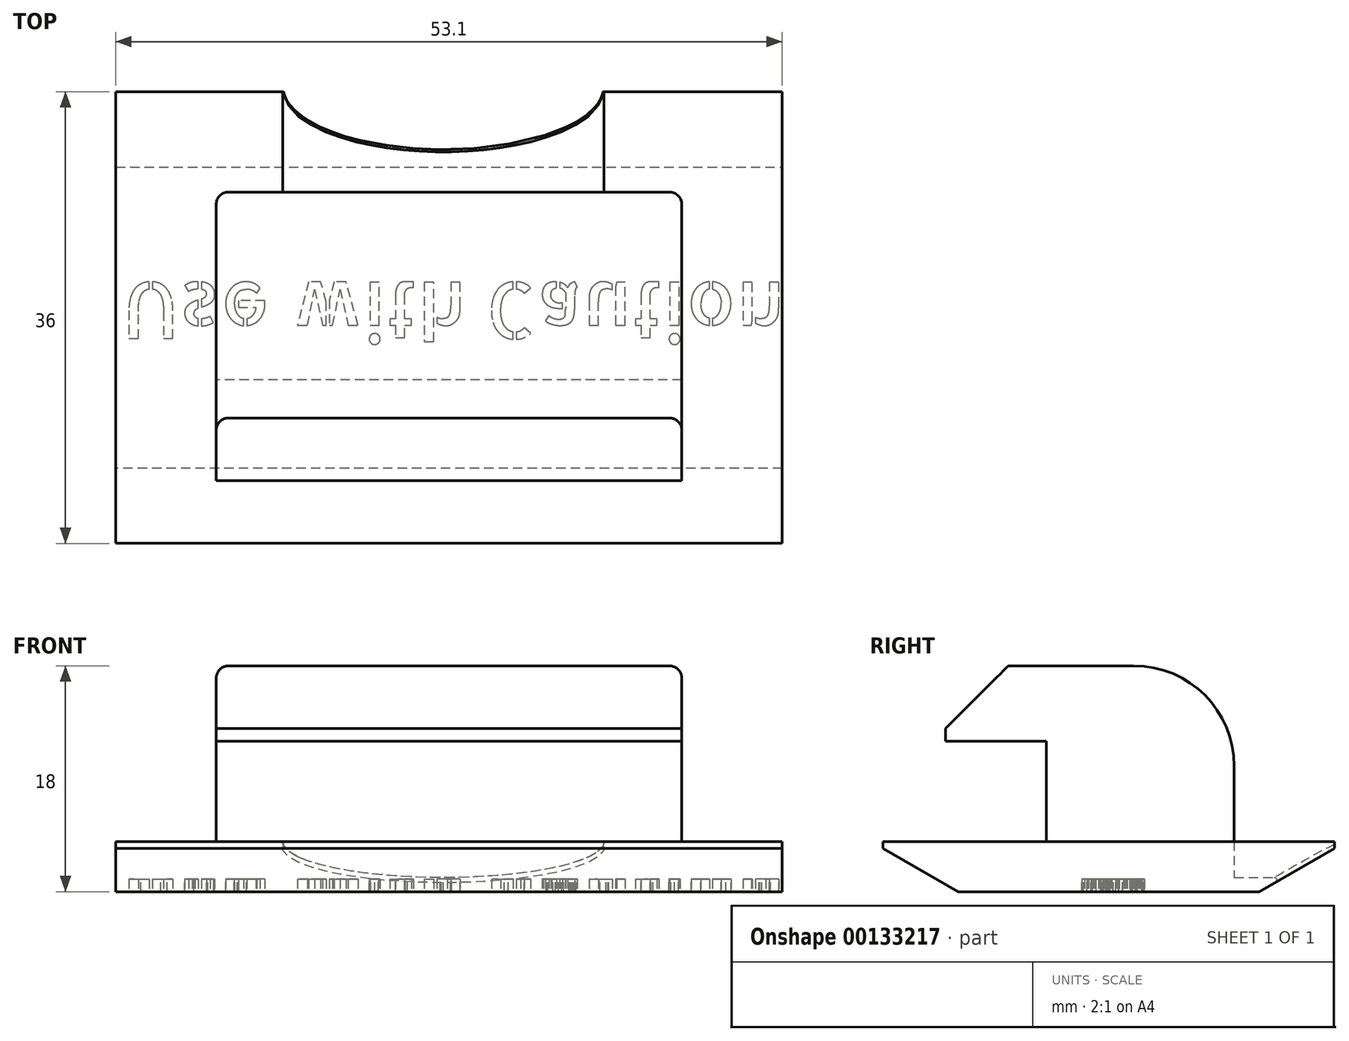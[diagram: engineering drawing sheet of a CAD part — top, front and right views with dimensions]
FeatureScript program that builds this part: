
annotation { "Feature Type Name" : "Feature", "Feature Type Description" : "" }
export const myFeature = defineFeature(function(context is Context, id is Id, definition is map)
    precondition{}
    {
        {
            var Q0;
            Q0=qCreatedBy(makeId("Top.planeOp"),FACE);
            var sketch = newSketch(context, id + "F0", { "sketchPlane" : qUnion([Q0])});
            skLineSegment(sketch, "E0.bottom", {"start": v(-18.1, 7.47) * mm, "end": v(19, 7.47) * mm});
            skLineSegment(sketch, "E0.top", {"start": v(-18.1, -12.53) * mm, "end": v(19, -12.53) * mm});
            skLineSegment(sketch, "E0.left", {"start": v(-18.1, 7.47) * mm, "end": v(-18.1, -12.53) * mm});
            skLineSegment(sketch, "E0.right", {"start": v(19, 7.47) * mm, "end": v(19, -12.53) * mm});
            skLineSegment(sketch, "E1.0", {"start": v(27, 15.47) * mm, "end": v(27, -20.53) * mm});
            skLineSegment(sketch, "E1.1", {"start": v(-26.1, 15.47) * mm, "end": v(27, 15.47) * mm});
            skLineSegment(sketch, "E1.2", {"start": v(-26.1, 15.47) * mm, "end": v(-26.1, -20.53) * mm});
            skLineSegment(sketch, "E1.3", {"start": v(-26.1, -20.53) * mm, "end": v(27, -20.53) * mm});
            skSolve(sketch);
        }
        {
            var Q0;
            Q0=makeQuery(id+"F0.imprint","IMPRINT",FACE,{"disambiguationData":[TD([[makeQuery(id+"F0.imprint","IMPRINT",EDGE,{"derivedFrom":sQuery(id+"F0.wireOp",EDGE,"E0.bottom")}),-1.0]])]});
            extrude(context, id + "F1", {"entities" : qUnion([Q0]), "depth" : 18 * mm});
        }
        {
            var Q0;
            Q0=makeQuery(id+"F0.imprint","IMPRINT",FACE,{"disambiguationData":[TD([[makeQuery(id+"F0.imprint","IMPRINT",EDGE,{"derivedFrom":sQuery(id+"F0.wireOp",EDGE,"E0.bottom")}),1.0]])]});
            extrude(context, id + "F2", {"entities" : qUnion([Q0]), "operationType" : NewBodyOperationType.ADD, "depth" : 4 * mm});
        }
        {
            var Q0;
            Q0=makeQuery(id+"F2.opExtrude","CAP_EDGE",EDGE,{"disambiguationData":[OSD([sQuery(id+"F0.wireOp",EDGE,"E1.1")])],"isStart":true});
            var Q1;
            Q1=makeQuery(id+"F2.opExtrude","CAP_EDGE",EDGE,{"disambiguationData":[OSD([sQuery(id+"F0.wireOp",EDGE,"E1.3")])],"isStart":true});
            chamfer(context, id + "F3", {"entities" : qUnion([Q0, Q1]), "chamferType" : ChamferType.OFFSET_ANGLE, "width" : 6 * mm, "oppositeDirection" : false, "angle" : 30 * degree, "tangentPropagation" : true});
        }
        {
            var Q0;
            Q0=makeQuery(id+"F1.opExtrude","SWEPT_FACE",FACE,{"disambiguationData":[OSD([sQuery(id+"F0.wireOp",EDGE,"E0.left")])]});
            var sketch = newSketch(context, id + "F4", { "sketchPlane" : qUnion([Q0])});
            skLineSegment(sketch, "E2.bottom", {"start": v(12.53, 12) * mm, "end": v(7.5, 12) * mm});
            skLineSegment(sketch, "E2.top", {"start": v(12.53, 4) * mm, "end": v(7.5, 4) * mm});
            skLineSegment(sketch, "E2.left", {"start": v(12.53, 12) * mm, "end": v(12.53, 4) * mm});
            skLineSegment(sketch, "E2.right", {"start": v(7.5, 12) * mm, "end": v(7.5, 4) * mm});
            skSolve(sketch);
        }
        {
            var Q0;
            Q0=makeQuery(id+"F4.imprint","IMPRINT",FACE,{"disambiguationData":[TD([[makeQuery(id+"F4.imprint","IMPRINT",EDGE,{"derivedFrom":sQuery(id+"F4.wireOp",EDGE,"E2.bottom")}),1.0]])]});
            extrude(context, id + "F5", {"entities" : qUnion([Q0]), "operationType" : NewBodyOperationType.REMOVE, "oppositeDirection" : true, "depth" : 40 * mm});
        }
        {
            var Q0;
            Q0=makeQuery(id+"F2.opExtrude","SWEPT_FACE",FACE,{"disambiguationData":[OSD([sQuery(id+"F0.wireOp",EDGE,"E1.1")])]});
            var sketch = newSketch(context, id + "F6", { "sketchPlane" : qUnion([Q0])});
            skEllipse(sketch, "E3", {"center": v(0, 4) * mm, "majorRadius": 12.8 * mm, "minorRadius": 2.88 * mm, "majorAxis": v(-1, 0)});
            skSolve(sketch);
        }
        {
            var Q0;
            {var subQ0=sQuery(id+"F6.wireOp",EDGE,"E3");var subQ1=sQuery(id+"F0.wireOp",EDGE,"E1.1");var subQ2=makeQuery(id+"F3.opChamfer","BLEND_EDGE",EDGE,{"blendedFrom":[makeQuery(id+"F2.opExtrude","CAP_EDGE",EDGE,{"disambiguationData":[OSD([subQ1])],"isStart":true}),makeQuery(id+"F2.opExtrude","SWEPT_FACE",FACE,{"disambiguationData":[OSD([subQ1])]})],"blendedInto":[makeQuery(id+"F2.opExtrude","SWEPT_FACE",FACE,{"disambiguationData":[OSD([subQ1])]})]});var subQ3=makeQuery(id+"F6.imprint","INTERSECT",VERTEX,{"disambiguationData":[OD(0.0)],"derivedFrom":[subQ2,subQ0]});Q0=makeQuery(id+"F6.imprint","IMPRINT",FACE,{"disambiguationData":[TD([[makeQuery(id+"F6.imprint","IMPRINT",EDGE,{"disambiguationData":[TD([[subQ3,-1.0]])],"derivedFrom":subQ0}),1.0]])]});}
            var Q1;
            {var subQ0=sQuery(id+"F6.wireOp",EDGE,"E3");var subQ1=sQuery(id+"F0.wireOp",EDGE,"E1.1");var subQ4=makeQuery(id+"F2.opExtrude","CAP_EDGE",EDGE,{"disambiguationData":[OSD([subQ1])],"isStart":false});var subQ5=makeQuery(id+"F6.imprint","INTERSECT",VERTEX,{"disambiguationData":[OD(0.0)],"derivedFrom":[subQ4,subQ0]});Q1=makeQuery(id+"F6.imprint","IMPRINT",FACE,{"disambiguationData":[TD([[makeQuery(id+"F6.imprint","IMPRINT",EDGE,{"disambiguationData":[TD([[subQ5,1.0]])],"derivedFrom":subQ4}),1.0]])]});}
            extrude(context, id + "F7", {"entities" : qUnion([Q0, Q1]), "operationType" : NewBodyOperationType.REMOVE, "oppositeDirection" : true, "depth" : 8 * mm});
        }
        {
            var Q0;
            Q0=makeQuery(id+"F1.opExtrude","SWEPT_FACE",FACE,{"disambiguationData":[OSD([sQuery(id+"F0.wireOp",EDGE,"E0.top")])]});
            extrude(context, id + "F8", {"entities" : qUnion([Q0]), "operationType" : NewBodyOperationType.ADD, "depth" : 3 * mm});
        }
        {
            var Q0;
            Q0=makeQuery(id+"F8.opExtrude","CAP_EDGE",EDGE,{"disambiguationData":[OSD([sQuery(id+"F0.wireOp",EDGE,"E0.top")])],"isStart":false});
            chamfer(context, id + "F9", {"entities" : qUnion([Q0]), "width" : 5 * mm, "tangentPropagation" : true});
        }
        {
            var Q0;
            Q0=makeQuery(id+"F1.opExtrude","CAP_EDGE",EDGE,{"disambiguationData":[OSD([sQuery(id+"F0.wireOp",EDGE,"E0.bottom")])],"isStart":false});
            fillet(context, id + "F10", {"entities" : qUnion([Q0]), "radius" : 8 * mm, "tangentPropagation" : true, "allowEdgeOverflow" : false});
        }
        {
            var Q0;
            {var subQ0=sQuery(id+"F0.wireOp",EDGE,"E0.right");var subQ1=sQuery(id+"F0.wireOp",EDGE,"E0.left");var subQ2=sQuery(id+"F0.wireOp",EDGE,"E0.top");var subQ3=sQuery(id+"F0.wireOp",EDGE,"E0.bottom");Q0=makeQuery(id+"F2.boolean.opBoolean","MERGE",FACE,{"derivedFrom":[makeQuery(id+"F1.opExtrude","CAP_FACE",FACE,{"disambiguationData":[OSD([subQ3,subQ2,subQ1,subQ0])],"isStart":true}),makeQuery(id+"F2.opExtrude","CAP_FACE",FACE,{"disambiguationData":[OSD([subQ3,subQ2,subQ1,subQ0,sQuery(id+"F0.wireOp",EDGE,"E1.0"),sQuery(id+"F0.wireOp",EDGE,"E1.1"),sQuery(id+"F0.wireOp",EDGE,"E1.2"),sQuery(id+"F0.wireOp",EDGE,"E1.3")])],"isStart":true})]});}
            var sketch = newSketch(context, id + "F11", { "sketchPlane" : qUnion([Q0])});
            skText(sketch, "E4", { "text": "Use with Caution\n", "fontName": "AllertaStencil-Regular.ttf"});
            const initialGuessF11  = {"E4": [-0.02555, -0.0003, 1, 0, 0.0045]};
            skSetInitialGuess(sketch, initialGuessF11);
            skSolve(sketch);
        }
        {
            var Q0;
            Q0 = qSketchRegion(id + "F11", true);
            extrude(context, id + "F12", {"entities" : qUnion([Q0]), "operationType" : NewBodyOperationType.REMOVE, "oppositeDirection" : true, "depth" : 1 * mm});
        }
        {
            var Q0;
            Q0=makeQuery(id+"F1.opExtrude","SWEPT_EDGE",EDGE,{"disambiguationData":[OSD([sQuery(id+"F0.wireOp",EDGE,"E0.bottom"),sQuery(id+"F0.wireOp",EDGE,"E0.right")])]});
            var Q1;
            Q1=makeQuery(id+"F1.opExtrude","CAP_EDGE",EDGE,{"disambiguationData":[OSD([sQuery(id+"F0.wireOp",EDGE,"E0.right")])],"isStart":false});
            var Q2;
            Q2=makeQuery(id+"F1.opExtrude","CAP_EDGE",EDGE,{"disambiguationData":[OSD([sQuery(id+"F0.wireOp",EDGE,"E0.bottom")])],"isStart":false});
            var Q3;
            Q3=makeQuery(id+"F1.opExtrude","SWEPT_EDGE",EDGE,{"disambiguationData":[OSD([sQuery(id+"F0.wireOp",EDGE,"E0.bottom"),sQuery(id+"F0.wireOp",EDGE,"E0.left")])]});
            var Q4;
            Q4=makeQuery(id+"F1.opExtrude","CAP_EDGE",EDGE,{"disambiguationData":[OSD([sQuery(id+"F0.wireOp",EDGE,"E0.left")])],"isStart":false});
            var Q5;
            Q5=makeQuery(id+"F1.opExtrude","CAP_EDGE",EDGE,{"disambiguationData":[OSD([sQuery(id+"F0.wireOp",EDGE,"E0.top")])],"isStart":false});
            var Q6;
            Q6=makeQuery(id+"F1.opExtrude","SWEPT_EDGE",EDGE,{"disambiguationData":[OSD([sQuery(id+"F0.wireOp",EDGE,"E0.top"),sQuery(id+"F0.wireOp",EDGE,"E0.left")])]});
            var Q7;
            Q7=makeQuery(id+"F1.opExtrude","SWEPT_EDGE",EDGE,{"disambiguationData":[OSD([sQuery(id+"F0.wireOp",EDGE,"E0.top"),sQuery(id+"F0.wireOp",EDGE,"E0.right")])]});
            fillet(context, id + "F13", {"entities" : qUnion([Q0, Q1, Q2, Q3, Q4, Q5, Q6, Q7]), "radius" : (1) * mm, "tangentPropagation" : true, "allowEdgeOverflow" : false});
        }
        {
            var Q0;
            Q0=makeQuery(id+"F7.boolean.opBoolean","INTERSECT",EDGE,{"derivedFrom":[makeQuery(id+"F3.opChamfer","BLEND_FACE",FACE,{"disambiguationData":[OSD([sQuery(id+"F0.wireOp",EDGE,"E1.1")])]}),makeQuery(id+"F7.opExtrude","SWEPT_FACE",FACE,{"disambiguationData":[OSD([sQuery(id+"F6.wireOp",EDGE,"E3")])]})]});
            fillet(context, id + "F14", {"entities" : qUnion([Q0]), "radius" : .2 * mm, "tangentPropagation" : true, "allowEdgeOverflow" : false});
        }
    });
